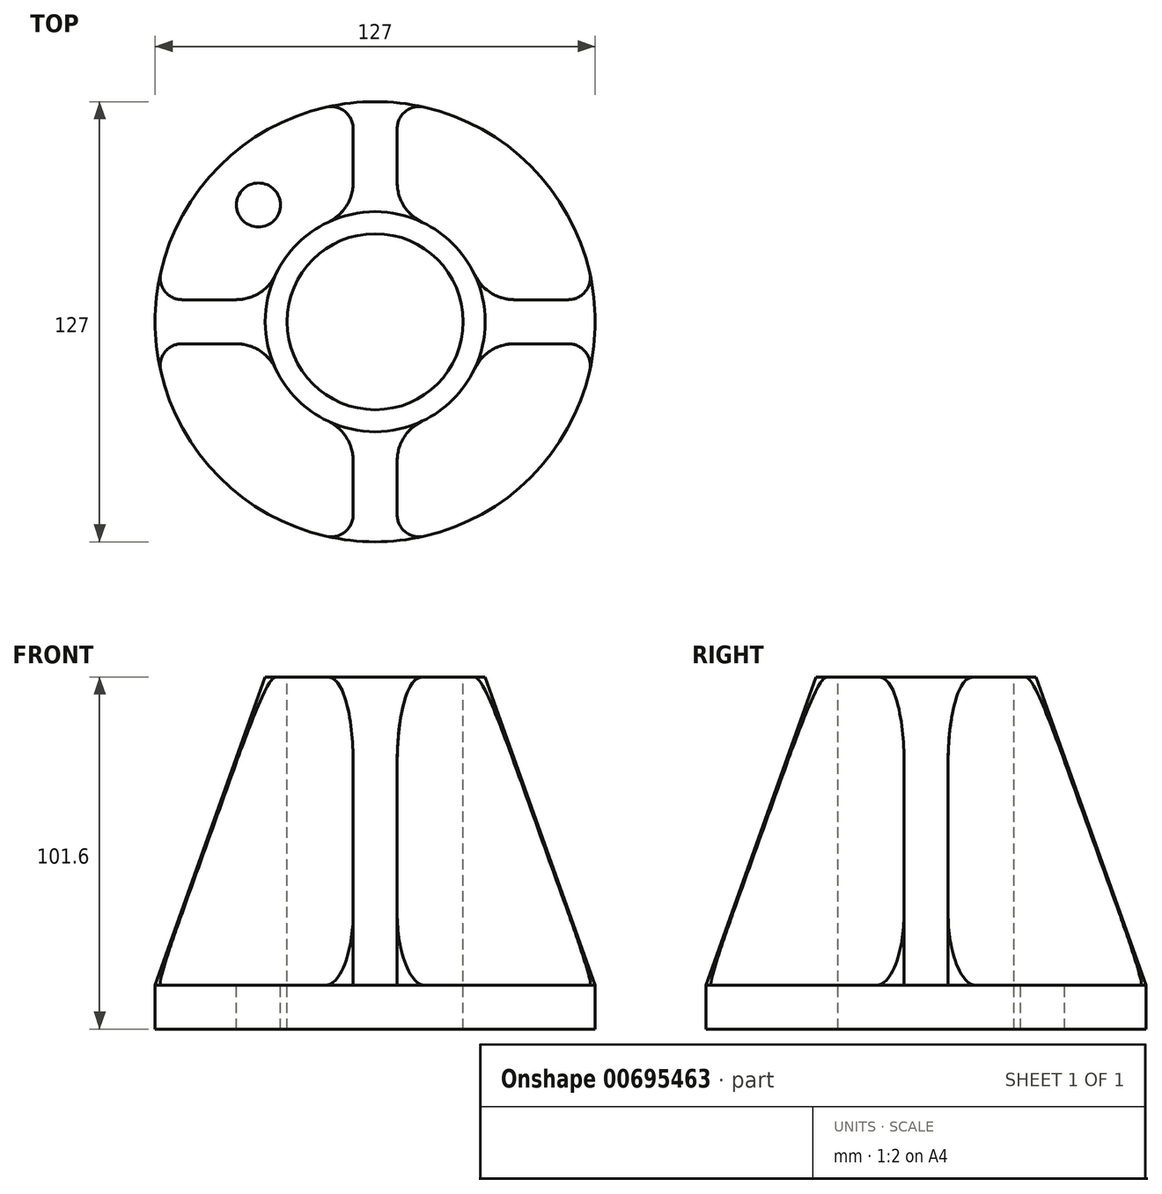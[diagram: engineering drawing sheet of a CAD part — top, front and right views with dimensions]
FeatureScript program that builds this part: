
annotation { "Feature Type Name" : "Feature", "Feature Type Description" : "" }
export const myFeature = defineFeature(function(context is Context, id is Id, definition is map)
    precondition{}
    {
        {
            var Q0;
            Q0=qCreatedBy(makeId("Top.planeOp"),FACE);
            var sketch = newSketch(context, id + "F0", { "sketchPlane" : qUnion([Q0])});
            skCircle(sketch, "E0", {"center": v(0, 0) * mm, "radius": 63.5 * mm});
            skSolve(sketch);
        }
        {
            var Q0;
            Q0=makeQuery(id+"F0.imprint","IMPRINT",FACE,{"disambiguationData":[TD([[makeQuery(id+"F0.imprint","IMPRINT",EDGE,{"derivedFrom":sQuery(id+"F0.wireOp",EDGE,"E0")}),1.0]])]});
            var Q1;
            Q1=sQuery(id+"F0.wireOp",EDGE,"E0");
            extrude(context, id + "F1", {"entities" : qUnion([Q0]), "surfaceEntities" : qUnion([Q1]), "depth" : 12.7 * mm, "offsetDistance" : 25.4 * mm});
        }
        {
            var Q0;
            Q0=makeQuery(id+"F1.opExtrude","CAP_FACE",FACE,{"disambiguationData":[OSD([sQuery(id+"F0.wireOp",EDGE,"E0")])],"isStart":false});
            var sketch = newSketch(context, id + "F2", { "sketchPlane" : qUnion([Q0])});
            skCircle(sketch, "E1", {"center": v(0, 0) * mm, "radius": 31.75 * mm});
            skSolve(sketch);
        }
        {
            var Q0;
            Q0=makeQuery(id+"F2.imprint","IMPRINT",FACE,{"disambiguationData":[TD([[makeQuery(id+"F2.imprint","IMPRINT",EDGE,{"derivedFrom":sQuery(id+"F2.wireOp",EDGE,"E1")}),1.0]])]});
            extrude(context, id + "F3", {"entities" : qUnion([Q0]), "operationType" : NewBodyOperationType.ADD, "depth" : 88.9 * mm, "offsetDistance" : 25.4 * mm});
        }
        {
            var Q0;
            Q0=qCreatedBy(makeId("Right.planeOp"),FACE);
            var sketch = newSketch(context, id + "F4", { "sketchPlane" : qUnion([Q0])});
            skLineSegment(sketch, "E2", {"start": v(-31.75, 101.6) * mm, "end": v(-63.5, 12.7) * mm});
            skLineSegment(sketch, "E3", {"start": v(-31.75, 12.7) * mm, "end": v(-31.75, 101.6) * mm});
            skLineSegment(sketch, "E4", {"start": v(-31.75, 12.7) * mm, "end": v(-63.5, 12.7) * mm});
            skLineSegment(sketch, "E5", {"start": v(0, 0) * mm, "end": v(0, 147.09) * mm, "construction": true});
            skSolve(sketch);
        }
        {
            var Q0;
            Q0=makeQuery(id+"F4.imprint","IMPRINT",FACE,{"disambiguationData":[TD([[makeQuery(id+"F4.imprint","IMPRINT",EDGE,{"derivedFrom":sQuery(id+"F4.wireOp",EDGE,"E2")}),1.0]])]});
            var Q1;
            Q1=sQuery(id+"F4.wireOp",EDGE,"E5");
            revolve(context, id + "F5", {"operationType" : NewBodyOperationType.ADD, "surfaceOperationType" : NewSurfaceOperationType.NEW, "entities" : qUnion([Q0]), "axis" : qUnion([Q1]), "revolveType" : RevolveType.FULL});
        }
        {
            var Q0;
            Q0=makeQuery(id+"F2.imprint","IMPRINT",FACE,{"disambiguationData":[TD([[makeQuery(id+"F2.imprint","IMPRINT",EDGE,{"derivedFrom":sQuery(id+"F2.wireOp",EDGE,"E1")}),-1.0]])]});
            var sketch = newSketch(context, id + "F6", { "sketchPlane" : qUnion([Q0])});
            skPoint(sketch, "E6.middle", {"position": v(0, 0) * mm});
            skArc(sketch, "E7", {"start": v(-61.91, 14.11) * mm, "mid": v(-60.69, 8.74) * mm, "end": v(-55.72, 6.35) * mm});
            skArc(sketch, "E8", {"start": v(-6.35, 55.72) * mm, "mid": v(-8.74, 60.69) * mm, "end": v(-14.11, 61.91) * mm});
            skArc(sketch, "E9.0", {"start": v(-13.6, 28.69) * mm, "mid": v(-22.45, 22.45) * mm, "end": v(-28.69, 13.6) * mm});
            skArc(sketch, "E10", {"start": v(-40.16, 6.35) * mm, "mid": v(-33.37, 8.32) * mm, "end": v(-28.69, 13.6) * mm});
            skArc(sketch, "E11", {"start": v(-13.6, 28.69) * mm, "mid": v(-8.32, 33.37) * mm, "end": v(-6.35, 40.16) * mm});
            skLineSegment(sketch, "E12", {"start": v(-55.72, 6.35) * mm, "end": v(-40.16, 6.35) * mm});
            skLineSegment(sketch, "E13", {"start": v(-6.35, 40.16) * mm, "end": v(-6.35, 55.72) * mm});
            skArc(sketch, "E14", {"start": v(-14.11, 61.91) * mm, "mid": v(-44.9, 44.9) * mm, "end": v(-61.91, 14.11) * mm});
            skArc(sketch, "E15.1.0", {"start": v(-55.72, -6.35) * mm, "mid": v(-60.69, -8.74) * mm, "end": v(-61.91, -14.11) * mm});
            skLineSegment(sketch, "E15.1.1", {"start": v(-6.35, -55.72) * mm, "end": v(-6.35, -40.16) * mm});
            skArc(sketch, "E15.1.2", {"start": v(-14.11, -61.91) * mm, "mid": v(-8.74, -60.69) * mm, "end": v(-6.35, -55.72) * mm});
            skArc(sketch, "E15.1.3", {"start": v(-28.69, -13.6) * mm, "mid": v(-33.37, -8.32) * mm, "end": v(-40.16, -6.35) * mm});
            skLineSegment(sketch, "E15.1.4", {"start": v(-40.16, -6.35) * mm, "end": v(-55.72, -6.35) * mm});
            skArc(sketch, "E15.1.5", {"start": v(-6.35, -40.16) * mm, "mid": v(-8.32, -33.37) * mm, "end": v(-13.6, -28.69) * mm});
            skArc(sketch, "E15.1.6", {"start": v(-61.91, -14.11) * mm, "mid": v(-44.9, -44.9) * mm, "end": v(-14.11, -61.91) * mm});
            skArc(sketch, "E15.1.8", {"start": v(-28.69, -13.6) * mm, "mid": v(-22.45, -22.45) * mm, "end": v(-13.6, -28.69) * mm});
            skArc(sketch, "E15.2.0", {"start": v(6.35, -55.72) * mm, "mid": v(8.74, -60.69) * mm, "end": v(14.11, -61.91) * mm});
            skLineSegment(sketch, "E15.2.1", {"start": v(55.72, -6.35) * mm, "end": v(40.16, -6.35) * mm});
            skArc(sketch, "E15.2.2", {"start": v(61.91, -14.11) * mm, "mid": v(60.69, -8.74) * mm, "end": v(55.72, -6.35) * mm});
            skArc(sketch, "E15.2.3", {"start": v(13.6, -28.69) * mm, "mid": v(8.32, -33.37) * mm, "end": v(6.35, -40.16) * mm});
            skLineSegment(sketch, "E15.2.4", {"start": v(6.35, -40.16) * mm, "end": v(6.35, -55.72) * mm});
            skArc(sketch, "E15.2.5", {"start": v(40.16, -6.35) * mm, "mid": v(33.37, -8.32) * mm, "end": v(28.69, -13.6) * mm});
            skArc(sketch, "E15.2.6", {"start": v(14.11, -61.91) * mm, "mid": v(44.9, -44.9) * mm, "end": v(61.91, -14.11) * mm});
            skArc(sketch, "E15.2.8", {"start": v(13.6, -28.69) * mm, "mid": v(22.45, -22.45) * mm, "end": v(28.69, -13.6) * mm});
            skArc(sketch, "E15.3.0", {"start": v(55.72, 6.35) * mm, "mid": v(60.69, 8.74) * mm, "end": v(61.91, 14.11) * mm});
            skLineSegment(sketch, "E15.3.1", {"start": v(6.35, 55.72) * mm, "end": v(6.35, 40.16) * mm});
            skArc(sketch, "E15.3.2", {"start": v(14.11, 61.91) * mm, "mid": v(8.74, 60.69) * mm, "end": v(6.35, 55.72) * mm});
            skArc(sketch, "E15.3.3", {"start": v(28.69, 13.6) * mm, "mid": v(33.37, 8.32) * mm, "end": v(40.16, 6.35) * mm});
            skLineSegment(sketch, "E15.3.4", {"start": v(40.16, 6.35) * mm, "end": v(55.72, 6.35) * mm});
            skArc(sketch, "E15.3.5", {"start": v(6.35, 40.16) * mm, "mid": v(8.32, 33.37) * mm, "end": v(13.6, 28.69) * mm});
            skArc(sketch, "E15.3.6", {"start": v(61.91, 14.11) * mm, "mid": v(44.9, 44.9) * mm, "end": v(14.11, 61.91) * mm});
            skArc(sketch, "E15.3.8", {"start": v(28.69, 13.6) * mm, "mid": v(22.45, 22.45) * mm, "end": v(13.6, 28.69) * mm});
            skSolve(sketch);
        }
        {
            var Q0;
            Q0 = qSketchRegion(id + "F6", true);
            extrude(context, id + "F7", {"entities" : qUnion([Q0]), "operationType" : NewBodyOperationType.REMOVE, "endBound" : BoundingType.UP_TO_NEXT, "depth" : 25.4 * mm, "offsetDistance" : 25.4 * mm});
        }
        {
            var Q0;
            Q0=makeQuery(id+"F2.imprint","IMPRINT",FACE,{"disambiguationData":[TD([[makeQuery(id+"F2.imprint","IMPRINT",EDGE,{"derivedFrom":sQuery(id+"F2.wireOp",EDGE,"E1")}),-1.0]])]});
            var sketch = newSketch(context, id + "F8", { "sketchPlane" : qUnion([Q0])});
            skCircle(sketch, "E16", {"center": v(-33.68, 33.68) * mm, "radius": 6.35 * mm});
            skLineSegment(sketch, "E17", {"start": v(0, 0) * mm, "end": v(-47.31, 47.31) * mm, "construction": true});
            skCircle(sketch, "E18.0", {"center": v(0, 0) * mm, "radius": 31.75 * mm, "construction": true});
            skCircle(sketch, "E19.0", {"center": v(0, 0) * mm, "radius": 63.5 * mm, "construction": true});
            skPoint(sketch, "E20", {"position": v(-22.45, 22.45) * mm});
            skPoint(sketch, "E21", {"position": v(-44.9, 44.9) * mm});
            skSolve(sketch);
        }
        {
            var Q0;
            Q0=makeQuery(id+"F8.imprint","IMPRINT",FACE,{"disambiguationData":[TD([[makeQuery(id+"F8.imprint","IMPRINT",EDGE,{"derivedFrom":sQuery(id+"F8.wireOp",EDGE,"E16")}),1.0]])]});
            extrude(context, id + "F9", {"entities" : qUnion([Q0]), "operationType" : NewBodyOperationType.REMOVE, "endBound" : BoundingType.THROUGH_ALL, "oppositeDirection" : true, "depth" : 25.4 * mm, "offsetDistance" : 25.4 * mm});
        }
        {
            var Q0;
            Q0=makeQuery(id+"F3.opExtrude","CAP_FACE",FACE,{"disambiguationData":[OSD([sQuery(id+"F2.wireOp",EDGE,"E1")])],"isStart":false});
            var sketch = newSketch(context, id + "F10", { "sketchPlane" : qUnion([Q0])});
            skCircle(sketch, "E22", {"center": v(0, 0) * mm, "radius": 25.4 * mm});
            skSolve(sketch);
        }
        {
            var Q0;
            Q0=makeQuery(id+"F10.imprint","IMPRINT",FACE,{"disambiguationData":[TD([[makeQuery(id+"F10.imprint","IMPRINT",EDGE,{"derivedFrom":sQuery(id+"F10.wireOp",EDGE,"E22")}),1.0]])]});
            extrude(context, id + "F11", {"entities" : qUnion([Q0]), "operationType" : NewBodyOperationType.REMOVE, "endBound" : BoundingType.THROUGH_ALL, "oppositeDirection" : true, "depth" : 25.4 * mm, "offsetDistance" : 25.4 * mm});
        }
    });
